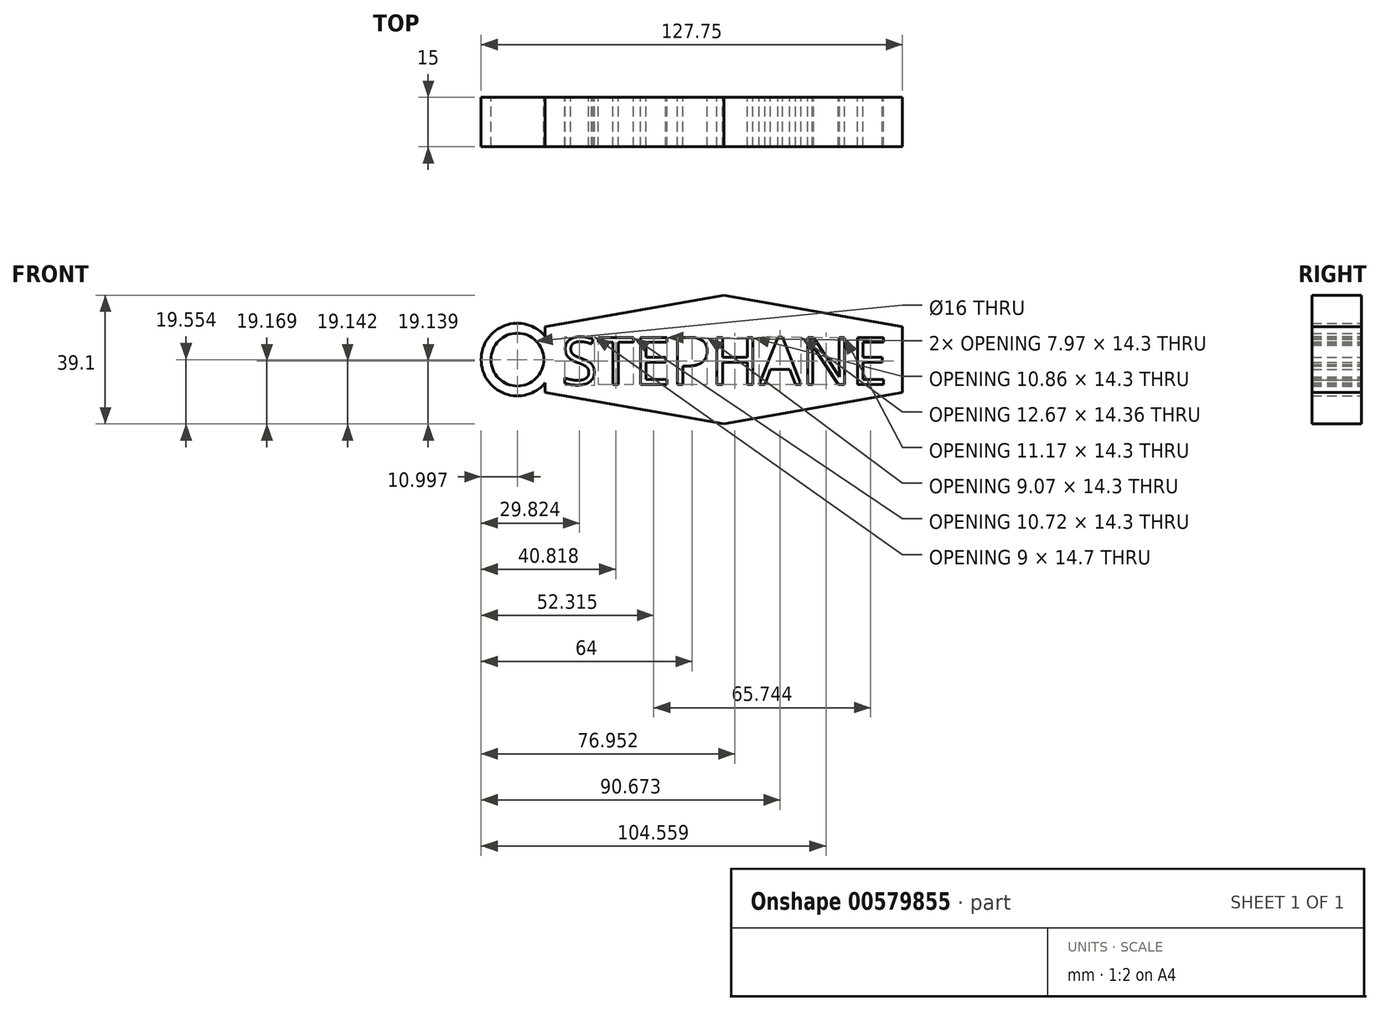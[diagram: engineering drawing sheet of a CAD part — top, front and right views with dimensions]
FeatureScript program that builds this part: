
annotation { "Feature Type Name" : "Feature", "Feature Type Description" : "" }
export const myFeature = defineFeature(function(context is Context, id is Id, definition is map)
    precondition{}
    {
        {
            var Q0;
            Q0=qCreatedBy(makeId("Front.planeOp"),FACE);
            var sketch = newSketch(context, id + "F0", { "sketchPlane" : qUnion([Q0])});
            skLineSegment(sketch, "E0", {"start": v(-75.92, 25.06) * mm, "end": v(-75.92, 5.06) * mm});
            skLineSegment(sketch, "E1", {"start": v(-75.92, 5.06) * mm, "end": v(-21.75, -4.49) * mm});
            skLineSegment(sketch, "E2", {"start": v(-21.75, -4.49) * mm, "end": v(32.41, 5.06) * mm});
            skLineSegment(sketch, "E3", {"start": v(32.41, 5.06) * mm, "end": v(32.41, 25.06) * mm});
            skLineSegment(sketch, "E4", {"start": v(32.41, 25.06) * mm, "end": v(-21.75, 34.61) * mm});
            skLineSegment(sketch, "E5", {"start": v(-21.75, 34.61) * mm, "end": v(-75.92, 25.06) * mm});
            skLineSegment(sketch, "E6", {"start": v(-75.92, 25.06) * mm, "end": v(-75.92, 15.06) * mm});
            skArc(sketch, "E7", {"start": v(-75.92, 22.14) * mm, "mid": v(-95.34, 15.06) * mm, "end": v(-75.92, 8) * mm});
            skCircle(sketch, "E8", {"center": v(-84.34, 15.06) * mm, "radius": 8 * mm});
            skText(sketch, "E9", { "text": "STEPHANE", "fontName": "OpenSans-Regular.ttf"});
            const initialGuessF0  = {"E9": [-0.07105, 0.0075, 1, 0, 0.01442]};
            skSetInitialGuess(sketch, initialGuessF0);
            skSolve(sketch);
        }
        {
            var Q0;
            {var subQ0=sQuery(id+"F0.wireOp",EDGE,"E1");Q0=makeQuery(id+"F0.imprint","IMPRINT",FACE,{"disambiguationData":[TD([[makeQuery(id+"F0.imprint","IMPRINT",EDGE,{"derivedFrom":subQ0}),1.0]])]});}
            var Q1;
            {var subQ3=sQuery(id+"F0.wireOp",EDGE,"E7");Q1=makeQuery(id+"F0.imprint","IMPRINT",FACE,{"disambiguationData":[TD([[makeQuery(id+"F0.imprint","IMPRINT",EDGE,{"derivedFrom":subQ3}),1.0]])]});}
            extrude(context, id + "F1", {"entities" : qUnion([Q0, Q1]), "depth" : 15 * mm, "offsetDistance" : 25 * mm});
        }
    });
